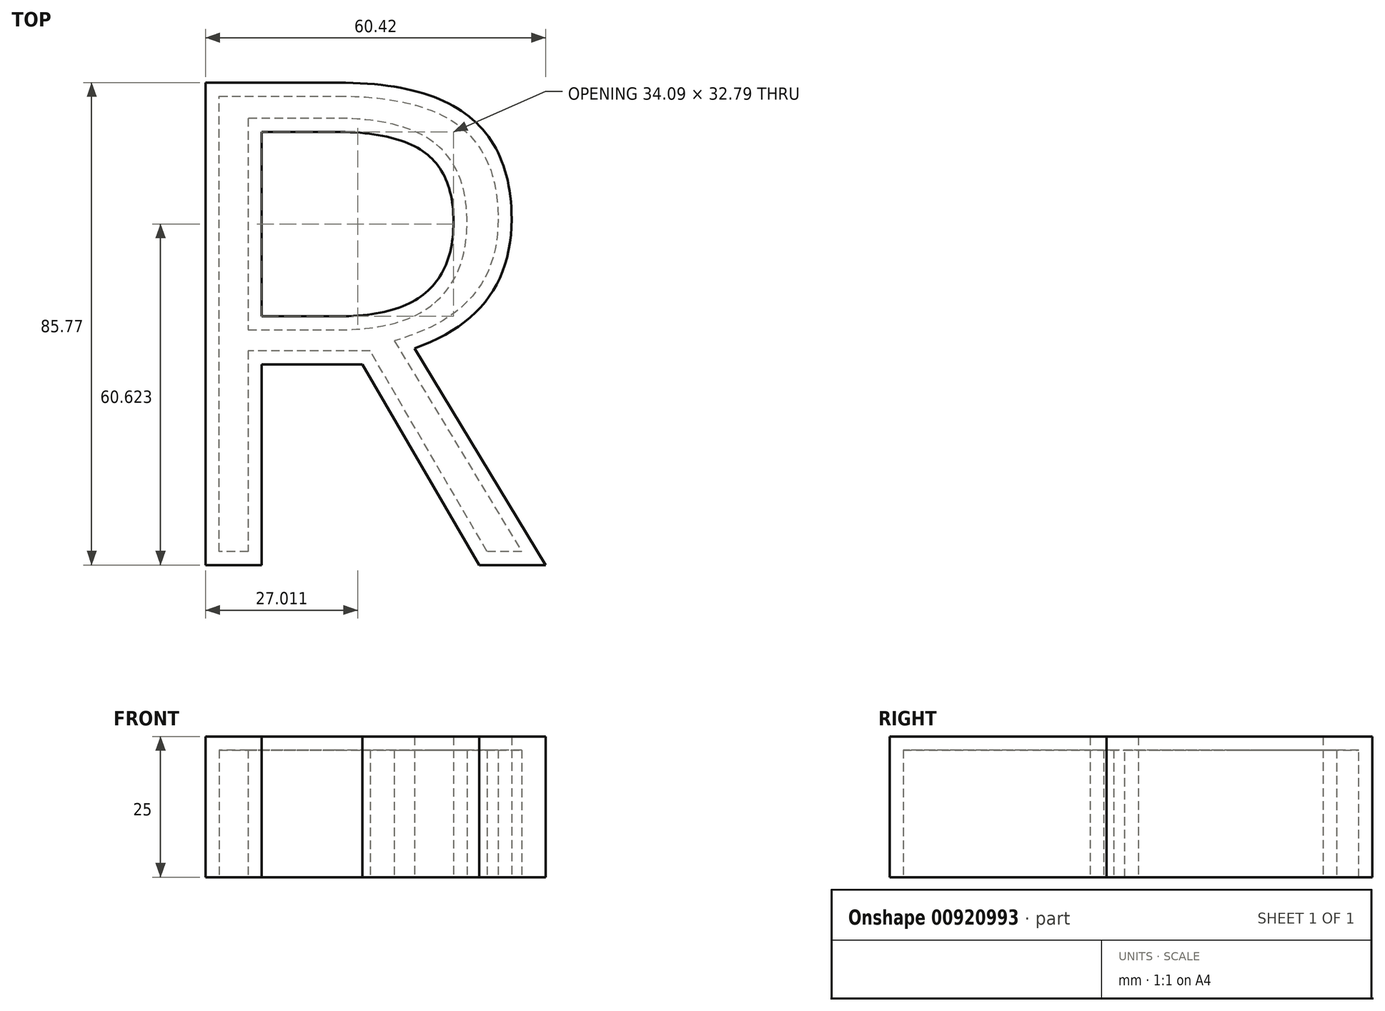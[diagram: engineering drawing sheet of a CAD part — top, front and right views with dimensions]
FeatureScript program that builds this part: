
annotation { "Feature Type Name" : "Feature", "Feature Type Description" : "" }
export const myFeature = defineFeature(function(context is Context, id is Id, definition is map)
    precondition{}
    {
        {
            var Q0;
            Q0=qCreatedBy(makeId("Top.planeOp"),FACE);
            var sketch = newSketch(context, id + "F0", { "sketchPlane" : qUnion([Q0])});
            skText(sketch, "E0", { "text": "R", "fontName": "OpenSans-Regular.ttf"});
            const initialGuessF0  = {"E0": [-0.03414, -0.04928, 1, 0, 0.0865]};
            skSetInitialGuess(sketch, initialGuessF0);
            skSolve(sketch);
        }
        {
            var Q0;
            Q0=makeQuery(id+"F0.imprint","IMPRINT",FACE,{"disambiguationData":[TD([[makeQuery(id+"F0.imprint","IMPRINT",EDGE,{"derivedFrom":sQuery(id+"F0.wireOp",EDGE,"E0.sketch_text.stroke-0")}),-1.0]])]});
            extrude(context, id + "F1", {"entities" : qUnion([Q0]), "depth" : 25 * mm, "offsetDistance" : 25 * mm});
        }
        {
            var Q0;
            Q0=makeQuery(id+"F1.opExtrude","CAP_FACE",FACE,{"disambiguationData":[OSD([sQuery(id+"F0.wireOp",EDGE,"E0.sketch_text.stroke-0"),sQuery(id+"F0.wireOp",EDGE,"E0.sketch_text.stroke-1"),sQuery(id+"F0.wireOp",EDGE,"E0.sketch_text.stroke-2"),sQuery(id+"F0.wireOp",EDGE,"E0.sketch_text.stroke-3"),sQuery(id+"F0.wireOp",EDGE,"E0.sketch_text.stroke-4"),sQuery(id+"F0.wireOp",EDGE,"E0.sketch_text.stroke-5"),sQuery(id+"F0.wireOp",EDGE,"E0.sketch_text.stroke-6"),sQuery(id+"F0.wireOp",EDGE,"E0.sketch_text.stroke-7"),sQuery(id+"F0.wireOp",EDGE,"E0.sketch_text.stroke-8"),sQuery(id+"F0.wireOp",EDGE,"E0.sketch_text.stroke-9"),sQuery(id+"F0.wireOp",EDGE,"E0.sketch_text.stroke-10"),sQuery(id+"F0.wireOp",EDGE,"E0.sketch_text.stroke-11"),sQuery(id+"F0.wireOp",EDGE,"E0.sketch_text.stroke-12"),sQuery(id+"F0.wireOp",EDGE,"E0.sketch_text.stroke-13"),sQuery(id+"F0.wireOp",EDGE,"E0.sketch_text.stroke-14"),sQuery(id+"F0.wireOp",EDGE,"E0.sketch_text.stroke-15"),sQuery(id+"F0.wireOp",EDGE,"E0.sketch_text.stroke-16"),sQuery(id+"F0.wireOp",EDGE,"E0.sketch_text.stroke-17")])],"isStart":true});
            shell(context, id + "F2", {"entities" : qUnion([Q0]), "thickness" : 2.4 * mm});
        }
    });
